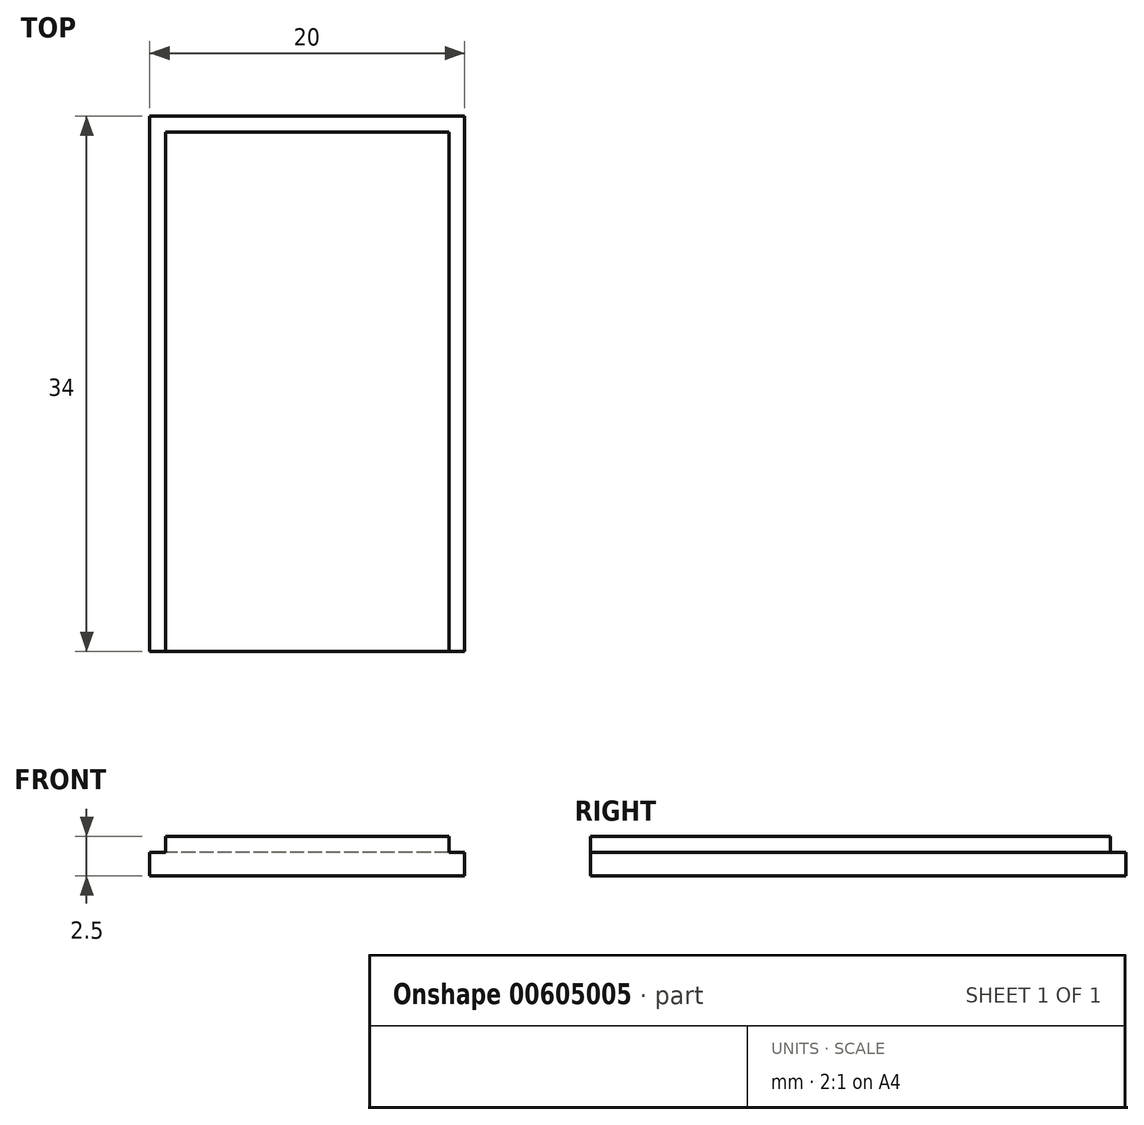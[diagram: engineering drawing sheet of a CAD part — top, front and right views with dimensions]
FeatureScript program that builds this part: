
annotation { "Feature Type Name" : "Feature", "Feature Type Description" : "" }
export const myFeature = defineFeature(function(context is Context, id is Id, definition is map)
    precondition{}
    {
        {
            var Q0;
            Q0=qCreatedBy(makeId("Front.planeOp"),FACE);
            var sketch = newSketch(context, id + "F0", { "sketchPlane" : qUnion([Q0])});
            skLineSegment(sketch, "E0", {"start": v(-10, 0) * mm, "end": v(10, 0) * mm});
            skLineSegment(sketch, "E1", {"start": v(10, 0) * mm, "end": v(10, 1.5) * mm});
            skLineSegment(sketch, "E2", {"start": v(10, 1.5) * mm, "end": v(9, 1.5) * mm});
            skLineSegment(sketch, "E3", {"start": v(9, 1.5) * mm, "end": v(9, 2.5) * mm});
            skLineSegment(sketch, "E4", {"start": v(9, 2.5) * mm, "end": v(-9, 2.5) * mm});
            skLineSegment(sketch, "E5", {"start": v(-9, 2.5) * mm, "end": v(-9, 1.5) * mm});
            skLineSegment(sketch, "E6", {"start": v(-9, 1.5) * mm, "end": v(-10, 1.5) * mm});
            skLineSegment(sketch, "E7", {"start": v(-10, 1.5) * mm, "end": v(-10, 0) * mm});
            skSolve(sketch);
        }
        {
            var Q0;
            Q0=makeQuery(id+"F0.imprint","IMPRINT",FACE,{"disambiguationData":[TD([[makeQuery(id+"F0.imprint","IMPRINT",EDGE,{"derivedFrom":sQuery(id+"F0.wireOp",EDGE,"E0")}),1.0]])]});
            extrude(context, id + "F1", {"entities" : qUnion([Q0]), "depth" : 34 * mm, "offsetDistance" : 25 * mm});
        }
        {
            var Q0;
            Q0=makeQuery(id+"F1.opExtrude","SWEPT_FACE",FACE,{"disambiguationData":[OSD([sQuery(id+"F0.wireOp",EDGE,"E5")])]});
            var sketch = newSketch(context, id + "F2", { "sketchPlane" : qUnion([Q0])});
            skLineSegment(sketch, "E8.bottom", {"start": v(0, 2.5) * mm, "end": v(1, 2.5) * mm});
            skLineSegment(sketch, "E8.top", {"start": v(0, 1.5) * mm, "end": v(1, 1.5) * mm});
            skLineSegment(sketch, "E8.left", {"start": v(0, 2.5) * mm, "end": v(0, 1.5) * mm});
            skLineSegment(sketch, "E8.right", {"start": v(1, 2.5) * mm, "end": v(1, 1.5) * mm});
            skSolve(sketch);
        }
        {
            var Q0;
            Q0 = qSketchRegion(id + "F2", true);
            extrude(context, id + "F3", {"entities" : qUnion([Q0]), "operationType" : NewBodyOperationType.REMOVE, "oppositeDirection" : true, "depth" : 25 * mm, "offsetDistance" : 25 * mm});
        }
    });
